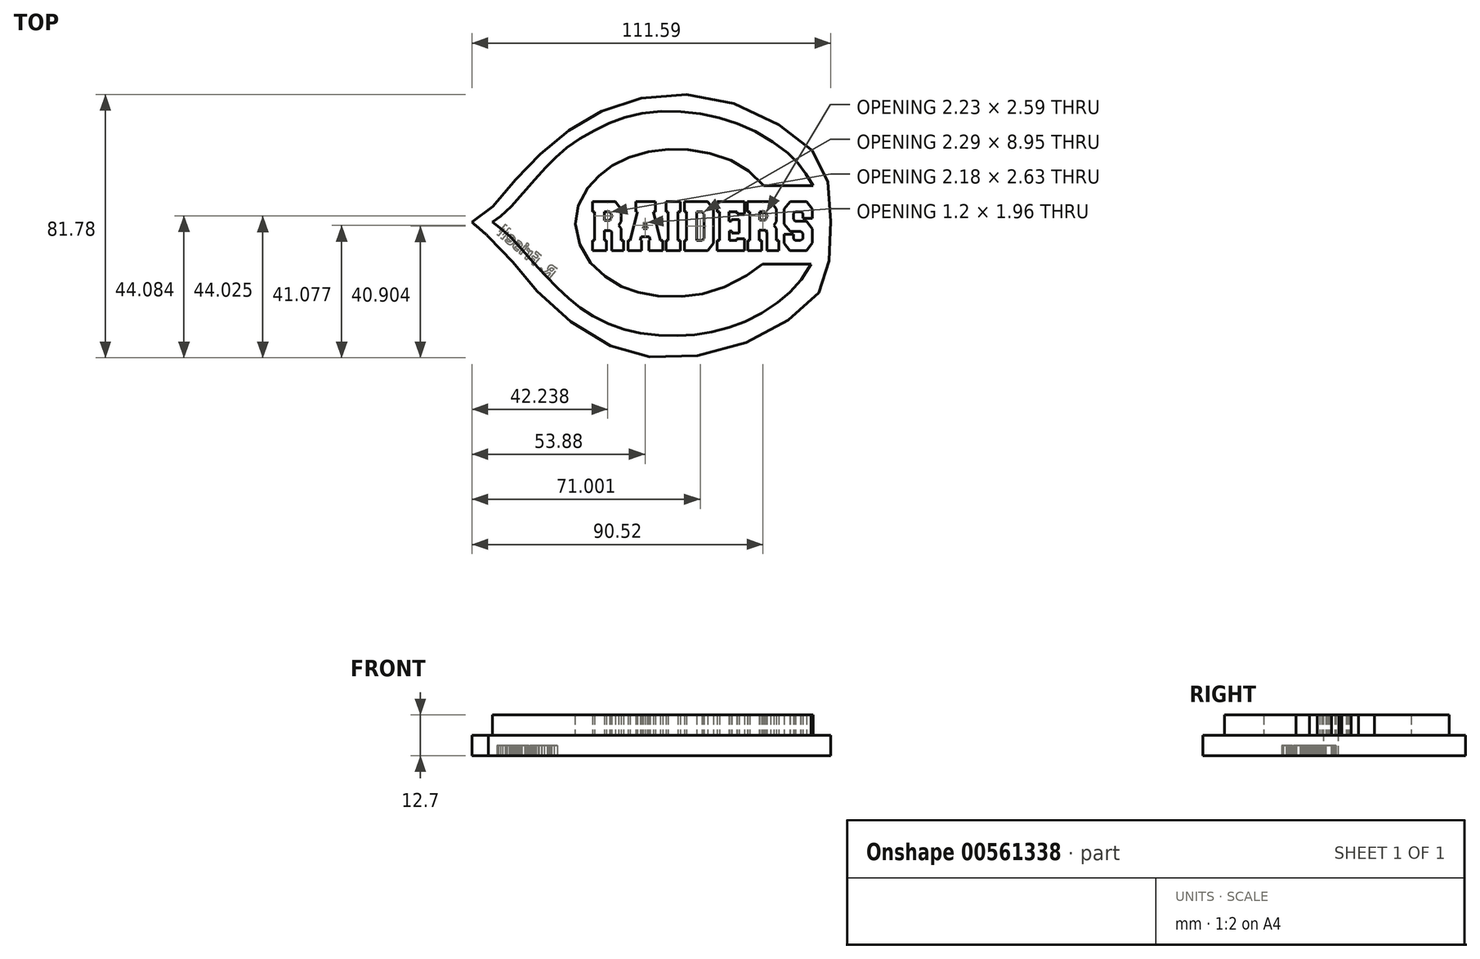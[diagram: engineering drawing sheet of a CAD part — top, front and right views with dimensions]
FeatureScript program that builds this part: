
annotation { "Feature Type Name" : "Feature", "Feature Type Description" : "" }
export const myFeature = defineFeature(function(context is Context, id is Id, definition is map)
    precondition{}
    {
        {
            var Q0;
            Q0=qCreatedBy(makeId("Top.planeOp"),FACE);
            var sketch = newSketch(context, id + "F0", { "sketchPlane" : qUnion([Q0])});
            skFitSpline(sketch, "E0", {"points": [v(-57.4, 1.5) * mm, v(-54.57, 3.48) * mm, v(-48.4, 9.87) * mm, v(-41.8, 17.47) * mm, v(-36.75, 22.5) * mm, v(-30.22, 27.4) * mm, v(-21.98, 31.8) * mm, v(-13.04, 34.86) * mm, v(-0.83, 35.93) * mm, v(11.88, 34.22) * mm, v(23.6, 29.96) * mm, v(34.38, 22.93) * mm, v(38.93, 18.04) * mm, v(42.26, 12.78) * mm], "startDerivative": vector(55.15, 33.66) * mm, "endDerivative": vector(50.55, -84.69) * mm});
            skLineSegment(sketch, "E1", {"start": v(42.26, 12.78) * mm, "end": v(26.93, 12.78) * mm});
            skLineSegment(sketch, "E2", {"start": v(26.5, -11.64) * mm, "end": v(41.63, -11.64) * mm});
            skFitSpline(sketch, "E3", {"points": [v(26.5, -11.64) * mm, v(20.9, -15.62) * mm, v(10.74, -20.16) * mm, v(3.43, -21.44) * mm, v(-6.37, -21.5) * mm, v(-13.04, -20.09) * mm, v(-18.36, -18.03) * mm, v(-23.97, -14.2) * mm, v(-28.8, -8.66) * mm, v(-31.5, -0.85) * mm, v(-31.21, 5.26) * mm, v(-28.16, 11.58) * mm, v(-24.68, 15.48) * mm, v(-21, 18.46) * mm, v(-15.8, 21.3) * mm, v(-8.7, 23.36) * mm, v(-1.6, 24.14) * mm, v(5.42, 23.79) * mm, v(14.44, 21.59) * mm, v(21.04, 18.18) * mm, v(26.93, 12.78) * mm], "startDerivative": vector(-101.24, -80.28) * mm, "endDerivative": vector(93, -113.22) * mm});
            skFitSpline(sketch, "E4", {"points": [v(-57.4, 1.5) * mm, v(-55.78, 0.22) * mm, v(-52.09, -2.9) * mm, v(-46.62, -8.87) * mm, v(-40.8, -15.26) * mm, v(-35.61, -20.51) * mm, v(-30.86, -24.63) * mm, v(-25.53, -28.04) * mm, v(-18, -31.45) * mm, v(-10.98, -33.08) * mm, v(-1.25, -33.86) * mm, v(6.84, -33.36) * mm, v(15.22, -31.59) * mm, v(22.67, -28.75) * mm, v(31.26, -23.57) * mm, v(36.44, -18.88) * mm, v(41.63, -11.64) * mm], "startDerivative": vector(44.5, -34.86) * mm, "endDerivative": vector(46.3, 111.1) * mm});
            skLineSegment(sketch, "E5", {"start": v(-26.35, 7.83) * mm, "end": v(-26.35, 4.66) * mm});
            skLineSegment(sketch, "E6", {"start": v(-26.35, 4.66) * mm, "end": v(-25.72, 4.66) * mm});
            skLineSegment(sketch, "E7", {"start": v(-25.72, 4.66) * mm, "end": v(-25.72, -4.23) * mm});
            skLineSegment(sketch, "E8", {"start": v(-25.72, -4.23) * mm, "end": v(-26.35, -4.23) * mm});
            skLineSegment(sketch, "E9", {"start": v(-26.35, -4.23) * mm, "end": v(-26.35, -7.34) * mm});
            skLineSegment(sketch, "E10", {"start": v(-26.35, -7.34) * mm, "end": v(-22, -7.34) * mm});
            skLineSegment(sketch, "E11", {"start": v(-22, -7.34) * mm, "end": v(-22, -4.23) * mm});
            skPoint(sketch, "E11.endSnap0", {"position": v(-26.03, -4.23) * mm});
            skLineSegment(sketch, "E12", {"start": v(-22, -4.23) * mm, "end": v(-22.67, -4.23) * mm});
            skLineSegment(sketch, "E13", {"start": v(-22.67, -4.23) * mm, "end": v(-22.67, -1.12) * mm});
            skLineSegment(sketch, "E14", {"start": v(-22.67, -1.12) * mm, "end": v(-20.86, -1.12) * mm});
            skLineSegment(sketch, "E15", {"start": v(-20.86, -1.12) * mm, "end": v(-20.38, -1.6) * mm});
            skLineSegment(sketch, "E16", {"start": v(-20.38, -1.6) * mm, "end": v(-20.38, -7.34) * mm});
            skLineSegment(sketch, "E17", {"start": v(-20.38, -7.34) * mm, "end": v(-16.7, -7.34) * mm});
            skLineSegment(sketch, "E18", {"start": v(-16.7, -7.34) * mm, "end": v(-16.7, -4.23) * mm});
            skLineSegment(sketch, "E19", {"start": v(-16.7, -4.23) * mm, "end": v(-17.36, -4.23) * mm});
            skLineSegment(sketch, "E20", {"start": v(-17.36, -4.23) * mm, "end": v(-17.36, -0.58) * mm});
            skLineSegment(sketch, "E21", {"start": v(-17.36, -0.58) * mm, "end": v(-18.18, 0.5) * mm});
            skLineSegment(sketch, "E22", {"start": v(-18.18, 0.5) * mm, "end": v(-17.38, 1.57) * mm});
            skLineSegment(sketch, "E23", {"start": v(-17.38, 1.57) * mm, "end": v(-17.38, 5.41) * mm});
            skLineSegment(sketch, "E24", {"start": v(-17.38, 5.41) * mm, "end": v(-19.22, 7.83) * mm});
            skLineSegment(sketch, "E25", {"start": v(-19.22, 7.83) * mm, "end": v(-26.35, 7.83) * mm});
            skLineSegment(sketch, "E26", {"start": v(-22.67, 2.05) * mm, "end": v(-22.67, 4.68) * mm});
            skLineSegment(sketch, "E27", {"start": v(-22.67, 4.68) * mm, "end": v(-20.97, 4.68) * mm});
            skLineSegment(sketch, "E28", {"start": v(-20.97, 4.68) * mm, "end": v(-20.5, 4.05) * mm});
            skLineSegment(sketch, "E29", {"start": v(-20.5, 4.05) * mm, "end": v(-20.5, 2.72) * mm});
            skLineSegment(sketch, "E30", {"start": v(-20.5, 2.72) * mm, "end": v(-21, 2.05) * mm});
            skLineSegment(sketch, "E31", {"start": v(-21, 2.05) * mm, "end": v(-22.67, 2.05) * mm});
            skLineSegment(sketch, "E32", {"start": v(-12.86, 7.83) * mm, "end": v(-12.86, 4.72) * mm});
            skLineSegment(sketch, "E33", {"start": v(-12.86, 4.72) * mm, "end": v(-12.3, 4.72) * mm});
            skLineSegment(sketch, "E34", {"start": v(-12.3, 4.72) * mm, "end": v(-14.62, -4.23) * mm});
            skPoint(sketch, "E34.endSnap0", {"position": v(-17.03, -4.23) * mm});
            skLineSegment(sketch, "E35", {"start": v(-14.62, -4.23) * mm, "end": v(-15.25, -4.23) * mm});
            skLineSegment(sketch, "E36", {"start": v(-15.25, -4.23) * mm, "end": v(-15.25, -7.34) * mm});
            skLineSegment(sketch, "E37", {"start": v(-15.25, -7.34) * mm, "end": v(-11.03, -7.34) * mm});
            skLineSegment(sketch, "E38", {"start": v(-11.03, -7.34) * mm, "end": v(-11.03, -4.23) * mm});
            skPoint(sketch, "E38.endSnap0", {"position": v(-14.94, -4.23) * mm});
            skLineSegment(sketch, "E39", {"start": v(-11.03, -4.23) * mm, "end": v(-11.43, -4.23) * mm});
            skLineSegment(sketch, "E40", {"start": v(-11.43, -4.23) * mm, "end": v(-11.22, -3.14) * mm});
            skLineSegment(sketch, "E41", {"start": v(-11.22, -3.14) * mm, "end": v(-8.63, -3.14) * mm});
            skLineSegment(sketch, "E42", {"start": v(-8.63, -3.14) * mm, "end": v(-8.34, -4.23) * mm});
            skLineSegment(sketch, "E43", {"start": v(-8.34, -4.23) * mm, "end": v(-8.8, -4.23) * mm});
            skLineSegment(sketch, "E44", {"start": v(-8.8, -4.23) * mm, "end": v(-8.8, -7.34) * mm});
            skLineSegment(sketch, "E45", {"start": v(-8.8, -7.34) * mm, "end": v(-4.52, -7.34) * mm});
            skLineSegment(sketch, "E46", {"start": v(-4.52, -7.34) * mm, "end": v(-4.52, -4.23) * mm});
            skLineSegment(sketch, "E47", {"start": v(-4.52, -4.23) * mm, "end": v(-5.25, -4.23) * mm});
            skLineSegment(sketch, "E48", {"start": v(-5.25, -4.23) * mm, "end": v(-7.38, 4.72) * mm});
            skPoint(sketch, "E48.endSnap0", {"position": v(-12.57, 4.72) * mm});
            skLineSegment(sketch, "E49", {"start": v(-7.38, 4.72) * mm, "end": v(-6.8, 4.72) * mm});
            skLineSegment(sketch, "E50", {"start": v(-6.8, 4.72) * mm, "end": v(-6.8, 7.83) * mm});
            skLineSegment(sketch, "E51", {"start": v(-6.8, 7.83) * mm, "end": v(-12.86, 7.83) * mm});
            skLineSegment(sketch, "E52", {"start": v(-10.54, -0.56) * mm, "end": v(-9.34, -0.56) * mm});
            skLineSegment(sketch, "E53", {"start": v(-9.34, -0.56) * mm, "end": v(-9.87, 1.4) * mm});
            skLineSegment(sketch, "E54", {"start": v(-9.87, 1.4) * mm, "end": v(-10.54, -0.56) * mm});
            skLineSegment(sketch, "E55", {"start": v(-2.76, -4.23) * mm, "end": v(-3.45, -4.23) * mm});
            skLineSegment(sketch, "E56", {"start": v(-3.45, -4.23) * mm, "end": v(-3.45, -7.34) * mm});
            skLineSegment(sketch, "E57", {"start": v(-3.45, -7.34) * mm, "end": v(0.99, -7.34) * mm});
            skLineSegment(sketch, "E58", {"start": v(0.99, -7.34) * mm, "end": v(0.99, -4.23) * mm});
            skLineSegment(sketch, "E59", {"start": v(0.99, -4.23) * mm, "end": v(0.3, -4.23) * mm});
            skLineSegment(sketch, "E60", {"start": v(0.3, -4.23) * mm, "end": v(0.3, 4.72) * mm});
            skLineSegment(sketch, "E61", {"start": v(0.3, 4.72) * mm, "end": v(0.94, 4.72) * mm});
            skLineSegment(sketch, "E62", {"start": v(0.94, 4.72) * mm, "end": v(0.94, 7.83) * mm});
            skLineSegment(sketch, "E63", {"start": v(0.94, 7.83) * mm, "end": v(-3.45, 7.83) * mm});
            skLineSegment(sketch, "E64", {"start": v(-3.45, 7.83) * mm, "end": v(-3.45, 4.72) * mm});
            skLineSegment(sketch, "E65", {"start": v(-3.45, 4.72) * mm, "end": v(-2.76, 4.72) * mm});
            skLineSegment(sketch, "E66", {"start": v(-2.76, 4.72) * mm, "end": v(-2.76, -4.23) * mm});
            skLineSegment(sketch, "E67", {"start": v(2.3, 7.83) * mm, "end": v(2.3, 4.72) * mm});
            skLineSegment(sketch, "E68", {"start": v(2.3, 4.72) * mm, "end": v(2.96, 4.72) * mm});
            skLineSegment(sketch, "E69", {"start": v(2.96, 4.72) * mm, "end": v(2.96, -4.23) * mm});
            skLineSegment(sketch, "E70", {"start": v(2.96, -4.23) * mm, "end": v(2.22, -4.23) * mm});
            skLineSegment(sketch, "E71", {"start": v(2.22, -4.23) * mm, "end": v(2.22, -7.34) * mm});
            skLineSegment(sketch, "E72", {"start": v(2.22, -7.34) * mm, "end": v(9.48, -7.34) * mm});
            skLineSegment(sketch, "E73", {"start": v(9.48, -7.34) * mm, "end": v(11.3, -5.07) * mm});
            skLineSegment(sketch, "E74", {"start": v(11.3, -5.07) * mm, "end": v(11.3, 5.42) * mm});
            skLineSegment(sketch, "E75", {"start": v(11.3, 5.42) * mm, "end": v(9.53, 7.83) * mm});
            skLineSegment(sketch, "E76", {"start": v(9.53, 7.83) * mm, "end": v(2.3, 7.83) * mm});
            skLineSegment(sketch, "E77", {"start": v(6.04, 4.72) * mm, "end": v(6.04, -4.23) * mm});
            skLineSegment(sketch, "E78", {"start": v(6.04, -4.23) * mm, "end": v(7.74, -4.23) * mm});
            skLineSegment(sketch, "E79", {"start": v(7.74, -4.23) * mm, "end": v(8.33, -3.6) * mm});
            skLineSegment(sketch, "E80", {"start": v(8.33, -3.6) * mm, "end": v(8.33, 3.96) * mm});
            skLineSegment(sketch, "E81", {"start": v(8.33, 3.96) * mm, "end": v(7.8, 4.72) * mm});
            skLineSegment(sketch, "E82", {"start": v(7.8, 4.72) * mm, "end": v(6.04, 4.72) * mm});
            skLineSegment(sketch, "E83", {"start": v(13.17, 4.72) * mm, "end": v(12.5, 4.72) * mm});
            skLineSegment(sketch, "E84", {"start": v(12.5, 4.72) * mm, "end": v(12.5, 7.83) * mm});
            skLineSegment(sketch, "E85", {"start": v(12.5, 7.83) * mm, "end": v(20.91, 7.83) * mm});
            skLineSegment(sketch, "E86", {"start": v(20.91, 7.83) * mm, "end": v(20.91, 4.08) * mm});
            skLineSegment(sketch, "E87", {"start": v(20.91, 4.08) * mm, "end": v(18.6, 4.08) * mm});
            skLineSegment(sketch, "E88", {"start": v(18.6, 4.08) * mm, "end": v(18.6, 4.72) * mm});
            skLineSegment(sketch, "E89", {"start": v(18.6, 4.72) * mm, "end": v(16.14, 4.72) * mm});
            skLineSegment(sketch, "E90", {"start": v(16.14, 4.72) * mm, "end": v(16.14, 1.72) * mm});
            skLineSegment(sketch, "E91", {"start": v(16.14, 1.72) * mm, "end": v(16.91, 1.72) * mm});
            skLineSegment(sketch, "E92", {"start": v(16.91, 1.72) * mm, "end": v(16.91, 2.27) * mm});
            skLineSegment(sketch, "E93", {"start": v(16.91, 2.27) * mm, "end": v(19.31, 2.27) * mm});
            skLineSegment(sketch, "E94", {"start": v(19.31, 2.27) * mm, "end": v(19.31, -1.98) * mm});
            skLineSegment(sketch, "E95", {"start": v(19.31, -1.98) * mm, "end": v(17, -1.98) * mm});
            skLineSegment(sketch, "E96", {"start": v(17, -1.98) * mm, "end": v(17, -1.33) * mm});
            skLineSegment(sketch, "E97", {"start": v(17, -1.33) * mm, "end": v(16.2, -1.33) * mm});
            skLineSegment(sketch, "E98", {"start": v(16.2, -1.33) * mm, "end": v(16.2, -4.23) * mm});
            skLineSegment(sketch, "E99", {"start": v(16.2, -4.23) * mm, "end": v(18.53, -4.23) * mm});
            skLineSegment(sketch, "E100", {"start": v(18.53, -4.23) * mm, "end": v(18.53, -3.66) * mm});
            skLineSegment(sketch, "E101", {"start": v(18.53, -3.66) * mm, "end": v(20.93, -3.66) * mm});
            skLineSegment(sketch, "E102", {"start": v(20.93, -3.66) * mm, "end": v(20.93, -7.34) * mm});
            skLineSegment(sketch, "E103", {"start": v(20.93, -7.34) * mm, "end": v(12.47, -7.34) * mm});
            skLineSegment(sketch, "E104", {"start": v(12.47, -7.34) * mm, "end": v(12.47, -4.23) * mm});
            skLineSegment(sketch, "E105", {"start": v(12.47, -4.23) * mm, "end": v(13.17, -4.23) * mm});
            skLineSegment(sketch, "E106", {"start": v(13.17, -4.23) * mm, "end": v(13.17, 4.72) * mm});
            skLineSegment(sketch, "E107", {"start": v(22.58, 4.72) * mm, "end": v(21.86, 4.72) * mm});
            skLineSegment(sketch, "E108", {"start": v(21.86, 4.72) * mm, "end": v(21.86, 7.83) * mm});
            skLineSegment(sketch, "E109", {"start": v(21.86, 7.83) * mm, "end": v(29.08, 7.83) * mm});
            skLineSegment(sketch, "E110", {"start": v(29.08, 7.83) * mm, "end": v(30.87, 5.54) * mm});
            skLineSegment(sketch, "E111", {"start": v(30.87, 5.54) * mm, "end": v(30.87, 1.65) * mm});
            skLineSegment(sketch, "E112", {"start": v(30.87, 1.65) * mm, "end": v(30.02, 0.51) * mm});
            skLineSegment(sketch, "E113", {"start": v(30.02, 0.51) * mm, "end": v(30.82, -0.56) * mm});
            skLineSegment(sketch, "E114", {"start": v(30.82, -0.56) * mm, "end": v(30.82, -4.23) * mm});
            skLineSegment(sketch, "E115", {"start": v(30.82, -4.23) * mm, "end": v(31.62, -4.23) * mm});
            skLineSegment(sketch, "E116", {"start": v(31.62, -4.23) * mm, "end": v(31.62, -7.34) * mm});
            skLineSegment(sketch, "E117", {"start": v(31.62, -7.34) * mm, "end": v(27.96, -7.34) * mm});
            skLineSegment(sketch, "E118", {"start": v(27.96, -7.34) * mm, "end": v(27.96, -1.65) * mm});
            skLineSegment(sketch, "E119", {"start": v(27.96, -1.65) * mm, "end": v(27.5, -1.09) * mm});
            skLineSegment(sketch, "E120", {"start": v(27.5, -1.09) * mm, "end": v(25.52, -1.09) * mm});
            skLineSegment(sketch, "E121", {"start": v(25.52, -1.09) * mm, "end": v(25.52, -4.23) * mm});
            skLineSegment(sketch, "E122", {"start": v(25.52, -4.23) * mm, "end": v(26.25, -4.23) * mm});
            skLineSegment(sketch, "E123", {"start": v(26.25, -4.23) * mm, "end": v(26.25, -7.34) * mm});
            skLineSegment(sketch, "E124", {"start": v(26.25, -7.34) * mm, "end": v(21.9, -7.34) * mm});
            skLineSegment(sketch, "E125", {"start": v(21.9, -7.34) * mm, "end": v(21.9, -4.23) * mm});
            skLineSegment(sketch, "E126", {"start": v(21.9, -4.23) * mm, "end": v(22.58, -4.23) * mm});
            skLineSegment(sketch, "E127", {"start": v(22.58, -4.23) * mm, "end": v(22.58, 4.72) * mm});
            skLineSegment(sketch, "E128", {"start": v(25.58, 4.72) * mm, "end": v(27.31, 4.72) * mm});
            skLineSegment(sketch, "E129", {"start": v(27.31, 4.72) * mm, "end": v(27.82, 4.15) * mm});
            skLineSegment(sketch, "E130", {"start": v(27.82, 4.15) * mm, "end": v(27.82, 2.63) * mm});
            skLineSegment(sketch, "E131", {"start": v(27.82, 2.63) * mm, "end": v(27.44, 2.13) * mm});
            skLineSegment(sketch, "E132", {"start": v(27.44, 2.13) * mm, "end": v(25.58, 2.13) * mm});
            skLineSegment(sketch, "E133", {"start": v(35.14, 7.83) * mm, "end": v(40.2, 7.83) * mm});
            skLineSegment(sketch, "E134", {"start": v(40.2, 7.83) * mm, "end": v(42.08, 5.5) * mm});
            skLineSegment(sketch, "E135", {"start": v(42.08, 5.5) * mm, "end": v(42.08, 2.62) * mm});
            skLineSegment(sketch, "E136", {"start": v(42.08, 2.62) * mm, "end": v(39.07, 2.62) * mm});
            skLineSegment(sketch, "E137", {"start": v(39.07, 2.62) * mm, "end": v(39.07, 4.1) * mm});
            skLineSegment(sketch, "E138", {"start": v(39.07, 4.1) * mm, "end": v(38.53, 4.66) * mm});
            skLineSegment(sketch, "E139", {"start": v(38.53, 4.66) * mm, "end": v(36.76, 4.66) * mm});
            skLineSegment(sketch, "E140", {"start": v(36.76, 4.66) * mm, "end": v(36.2, 4.11) * mm});
            skLineSegment(sketch, "E141", {"start": v(36.2, 4.11) * mm, "end": v(36.2, 2.39) * mm});
            skLineSegment(sketch, "E142", {"start": v(36.2, 2.39) * mm, "end": v(36.74, 1.72) * mm});
            skLineSegment(sketch, "E143", {"start": v(36.74, 1.72) * mm, "end": v(40.2, 1.72) * mm});
            skLineSegment(sketch, "E144", {"start": v(40.2, 1.72) * mm, "end": v(42.06, -0.61) * mm});
            skLineSegment(sketch, "E145", {"start": v(42.06, -0.61) * mm, "end": v(42.08, -4.99) * mm});
            skLineSegment(sketch, "E146", {"start": v(42.08, -4.99) * mm, "end": v(40.2, -7.43) * mm});
            skLineSegment(sketch, "E147", {"start": v(40.2, -7.43) * mm, "end": v(35.03, -7.43) * mm});
            skLineSegment(sketch, "E148", {"start": v(35.03, -7.43) * mm, "end": v(33.28, -5.14) * mm});
            skLineSegment(sketch, "E149", {"start": v(33.28, -5.14) * mm, "end": v(33.28, -2.32) * mm});
            skLineSegment(sketch, "E150", {"start": v(33.28, -2.32) * mm, "end": v(36.15, -2.32) * mm});
            skLineSegment(sketch, "E151", {"start": v(36.15, -2.32) * mm, "end": v(36.15, -3.67) * mm});
            skLineSegment(sketch, "E152", {"start": v(36.15, -3.67) * mm, "end": v(36.65, -4.21) * mm});
            skLineSegment(sketch, "E153", {"start": v(36.65, -4.21) * mm, "end": v(38.4, -4.21) * mm});
            skLineSegment(sketch, "E154", {"start": v(38.4, -4.21) * mm, "end": v(39.07, -3.67) * mm});
            skLineSegment(sketch, "E155", {"start": v(39.07, -3.67) * mm, "end": v(39.07, -2.02) * mm});
            skLineSegment(sketch, "E156", {"start": v(39.07, -2.02) * mm, "end": v(38.52, -1.44) * mm});
            skLineSegment(sketch, "E157", {"start": v(38.52, -1.44) * mm, "end": v(35.14, -1.44) * mm});
            skLineSegment(sketch, "E158", {"start": v(35.14, -1.44) * mm, "end": v(33.28, 0.85) * mm});
            skLineSegment(sketch, "E159", {"start": v(33.28, 0.85) * mm, "end": v(33.28, 5.54) * mm});
            skLineSegment(sketch, "E160", {"start": v(33.28, 5.54) * mm, "end": v(35.14, 7.83) * mm});
            skLineSegment(sketch, "E161", {"start": v(25.58, 4.72) * mm, "end": v(25.58, 2.13) * mm});
            skSolve(sketch);
        }
        {
            var Q0;
            Q0 = qSketchRegion(id + "F0", true);
            extrude(context, id + "F1", {"entities" : qUnion([Q0]), "depth" : 6.35 * mm, "offsetDistance" : 25.4 * mm});
        }
        {
            var Q0;
            Q0=makeQuery(id+"F1.opExtrude","CAP_FACE",FACE,{"disambiguationData":[OSD([sQuery(id+"F0.wireOp",EDGE,"E0"),sQuery(id+"F0.wireOp",EDGE,"E1"),sQuery(id+"F0.wireOp",EDGE,"E2"),sQuery(id+"F0.wireOp",EDGE,"E3"),sQuery(id+"F0.wireOp",EDGE,"E4")])],"isStart":true});
            var sketch = newSketch(context, id + "F2", { "sketchPlane" : qUnion([Q0])});
            skFitSpline(sketch, "E162", {"points": [v(-63.82, -1.53) * mm, v(-59.25, -4.6) * mm, v(-51.77, -12.73) * mm, v(-43.89, -21.34) * mm, v(-33.97, -29.8) * mm, v(-21.94, -36.62) * mm, v(-5.2, -40.85) * mm, v(15.69, -38.9) * mm, v(35.6, -29.06) * mm, v(45.2, -19.24) * mm, v(47.64, -6.72) * mm, v(47.44, 8.82) * mm, v(44.74, 19.39) * mm, v(33.16, 29.94) * mm, v(12.68, 38.8) * mm, v(-9.35, 40.26) * mm, v(-24.43, 35.12) * mm, v(-41.53, 22.3) * mm, v(-50.39, 11.6) * mm, v(-58.63, 3.05) * mm], "startDerivative": vector(108.98, -89.64) * mm, "endDerivative": vector(-108.2, -162.83) * mm});
            skFitSpline(sketch, "E163", {"points": [v(-58.63, 3.05) * mm, v(-63.82, -1.53) * mm], "startDerivative": vector(-3.17, -3.33) * mm, "endDerivative": vector(-3.17, -3.33) * mm});
            skSolve(sketch);
        }
        {
            var Q0;
            Q0 = qSketchRegion(id + "F2", true);
            extrude(context, id + "F3", {"entities" : qUnion([Q0]), "depth" : 6.35 * mm, "offsetDistance" : 25.4 * mm});
        }
        {
            var Q0;
            Q0=makeQuery(id+"F3.opExtrude","CAP_FACE",FACE,{"disambiguationData":[OSD([sQuery(id+"F2.wireOp",EDGE,"E162"),sQuery(id+"F2.wireOp",EDGE,"E163")])],"isStart":false});
            var sketch = newSketch(context, id + "F4", { "sketchPlane" : qUnion([Q0])});
            skText(sketch, "E164", { "text": "R. Frisell", "fontName": "OpenSans-Bold.ttf"});
            const initialGuessF4  = {"E164": [-0.03932, 0.01637, -0.76604, -0.64279, 0.00381]};
            skSetInitialGuess(sketch, initialGuessF4);
            skSolve(sketch);
        }
        {
            var Q0;
            Q0 = qSketchRegion(id + "F4", true);
            extrude(context, id + "F5", {"entities" : qUnion([Q0]), "operationType" : NewBodyOperationType.REMOVE, "oppositeDirection" : true, "depth" : 3.17 * mm, "offsetDistance" : 25.4 * mm});
        }
    });
